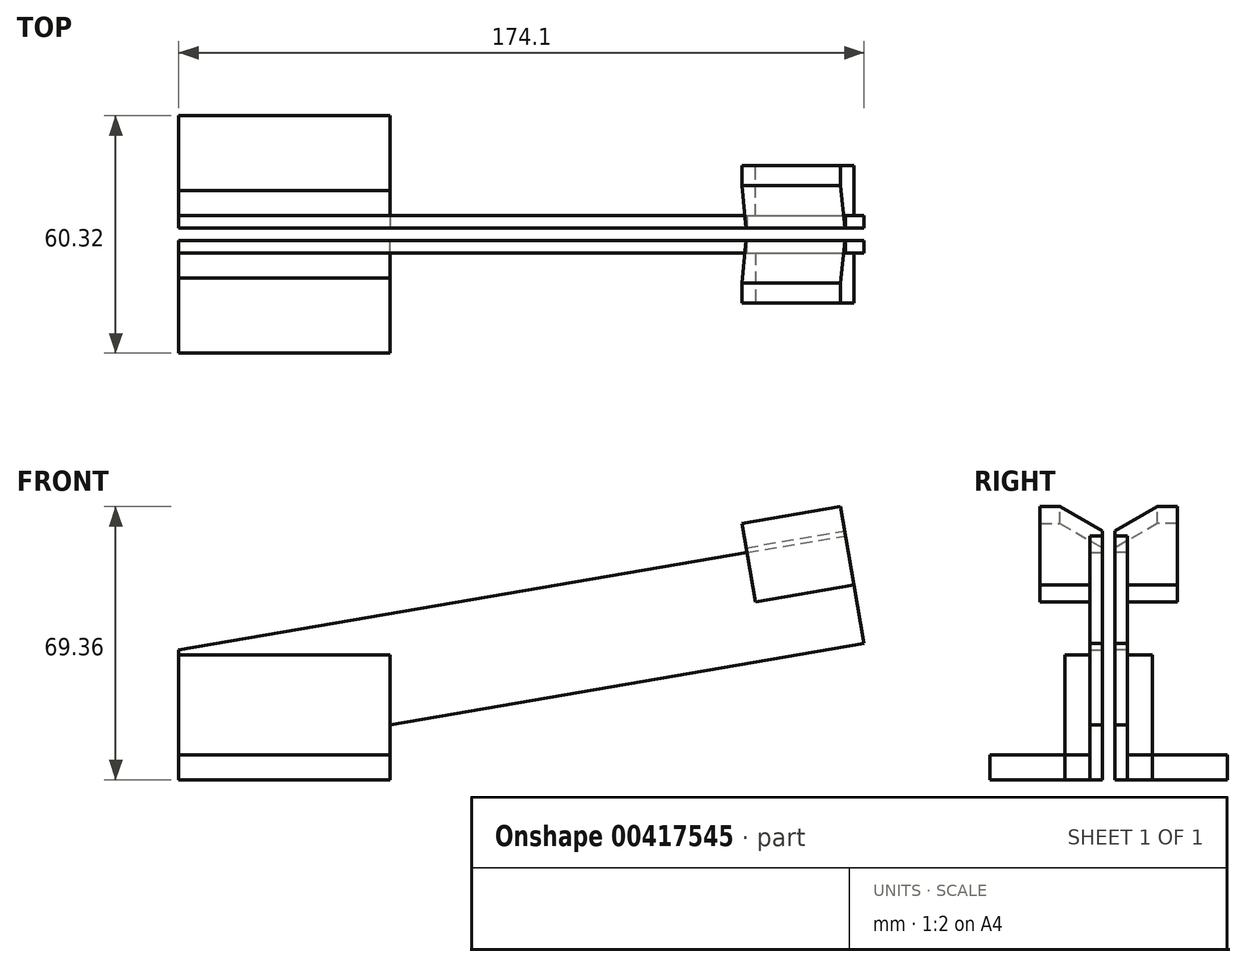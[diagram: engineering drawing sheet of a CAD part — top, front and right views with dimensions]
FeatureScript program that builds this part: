
annotation { "Feature Type Name" : "Feature", "Feature Type Description" : "" }
export const myFeature = defineFeature(function(context is Context, id is Id, definition is map)
    precondition{}
    {
        {
            var Q0;
            Q0=qCreatedBy(makeId("Front.planeOp"),FACE);
            var sketch = newSketch(context, id + "F0", { "sketchPlane" : qUnion([Q0])});
            skLineSegment(sketch, "E0", {"start": v(0, 0) * mm, "end": v(0, 33) * mm});
            skLineSegment(sketch, "E1", {"start": v(0, 33) * mm, "end": v(169.41, 61.97) * mm});
            skLineSegment(sketch, "E2", {"start": v(169.41, 61.97) * mm, "end": v(174.1, 34.58) * mm});
            skLineSegment(sketch, "E3", {"start": v(174.1, 34.58) * mm, "end": v(53.61, 13.97) * mm});
            skLineSegment(sketch, "E4", {"start": v(53.61, 13.97) * mm, "end": v(53.61, 0) * mm});
            skLineSegment(sketch, "E5", {"start": v(53.61, 0) * mm, "end": v(0, 0) * mm});
            skSolve(sketch);
        }
        {
            var Q0;
            Q0=makeQuery(id+"F0.imprint","IMPRINT",FACE,{"disambiguationData":[TD([[makeQuery(id+"F0.imprint","IMPRINT",EDGE,{"derivedFrom":sQuery(id+"F0.wireOp",EDGE,"E0")}),-1.0]])]});
            extrude(context, id + "F1", {"entities" : qUnion([Q0]), "depth" : 3.17 * mm});
        }
        {
            var Q0;
            Q0=makeQuery(id+"F1.opExtrude","SWEPT_FACE",FACE,{"disambiguationData":[OSD([sQuery(id+"F0.wireOp",EDGE,"E2")])]});
            var sketch = newSketch(context, id + "F2", { "sketchPlane" : qUnion([Q0])});
            skLineSegment(sketch, "E6", {"start": v(0, 32.52) * mm, "end": v(-3.18, 32.52) * mm});
            skLineSegment(sketch, "E7", {"start": v(-3.18, 32.52) * mm, "end": v(-3.17, 19.82) * mm});
            skLineSegment(sketch, "E8", {"start": v(-3.18, 19.82) * mm, "end": v(-15.88, 19.82) * mm});
            skLineSegment(sketch, "E9", {"start": v(-15.88, 19.82) * mm, "end": v(-15.88, 40.02) * mm});
            skLineSegment(sketch, "E10", {"start": v(-15.88, 40.02) * mm, "end": v(-10.8, 40.02) * mm});
            skLineSegment(sketch, "E11", {"start": v(-10.8, 40.02) * mm, "end": v(0, 33.79) * mm});
            skLineSegment(sketch, "E12", {"start": v(0, 33.79) * mm, "end": v(0, 32.52) * mm});
            skSolve(sketch);
        }
        {
            var Q0;
            Q0=makeQuery(id+"F2.imprint","IMPRINT",FACE,{"disambiguationData":[TD([[makeQuery(id+"F2.imprint","IMPRINT",EDGE,{"derivedFrom":sQuery(id+"F2.wireOp",EDGE,"E6")}),1.0]])]});
            extrude(context, id + "F3", {"entities" : qUnion([Q0]), "oppositeDirection" : true, "depth" : 25.4 * mm});
        }
        {
            var Q0;
            Q0=qCreatedBy(makeId("Front.planeOp"),FACE);
            cPlane(context, id + "F4", {"entities" : qUnion([Q0]), "cplaneType" : CPlaneType.OFFSET, "offset" : 1.59 * mm, "oppositeDirection" : true, "width" : 152.4 * mm, "height" : 152.4 * mm});
        }
        {
            var Q0;
            Q0=makeQuery(id+"F3.opExtrude","SWEPT_BODY",BODY,{"disambiguationData":[OSD([sQuery(id+"F2.wireOp",EDGE,"E6"),sQuery(id+"F2.wireOp",EDGE,"E7"),sQuery(id+"F2.wireOp",EDGE,"E8"),sQuery(id+"F2.wireOp",EDGE,"E9"),sQuery(id+"F2.wireOp",EDGE,"E10"),sQuery(id+"F2.wireOp",EDGE,"E11"),sQuery(id+"F2.wireOp",EDGE,"E12")])]});
            var Q1;
            Q1=makeQuery(id+"F1.opExtrude","SWEPT_BODY",BODY,{"disambiguationData":[OSD([sQuery(id+"F0.wireOp",EDGE,"E0"),sQuery(id+"F0.wireOp",EDGE,"E1"),sQuery(id+"F0.wireOp",EDGE,"E2"),sQuery(id+"F0.wireOp",EDGE,"E3"),sQuery(id+"F0.wireOp",EDGE,"E4"),sQuery(id+"F0.wireOp",EDGE,"E5")])]});
            var Q2;
            Q2=qCreatedBy(id+"F4.planeOp",FACE);
            mirror(context, id + "F5", {"entities" : qUnion([Q0, Q1]), "mirrorPlane" : qUnion([Q2])});
        }
        {
            var Q0;
            Q0=qCreatedBy(makeId("Top.planeOp"),FACE);
            var sketch = newSketch(context, id + "F6", { "sketchPlane" : qUnion([Q0])});
            skLineSegment(sketch, "E13.bottom", {"start": v(53.61, -28.57) * mm, "end": v(0, -28.57) * mm});
            skLineSegment(sketch, "E13.top", {"start": v(53.61, -3.18) * mm, "end": v(0, -3.18) * mm});
            skLineSegment(sketch, "E13.left", {"start": v(53.61, -28.58) * mm, "end": v(53.61, -3.18) * mm});
            skLineSegment(sketch, "E13.right", {"start": v(0, -28.57) * mm, "end": v(0, -3.18) * mm});
            skLineSegment(sketch, "E14.bottom", {"start": v(53.61, 31.75) * mm, "end": v(0, 31.75) * mm});
            skLineSegment(sketch, "E14.top", {"start": v(53.61, 6.35) * mm, "end": v(0, 6.35) * mm});
            skLineSegment(sketch, "E14.left", {"start": v(53.61, 31.75) * mm, "end": v(53.61, 6.35) * mm});
            skLineSegment(sketch, "E14.right", {"start": v(0, 31.75) * mm, "end": v(0, 6.35) * mm});
            skLineSegment(sketch, "E15", {"start": v(53.61, 12.7) * mm, "end": v(0, 12.7) * mm});
            skLineSegment(sketch, "E16", {"start": v(53.61, -9.53) * mm, "end": v(0, -9.53) * mm});
            skSolve(sketch);
        }
        {
            var Q0;
            Q0 = qSketchRegion(id + "F6", true);
            extrude(context, id + "F7", {"entities" : qUnion([Q0]), "depth" : 6.35 * mm});
        }
        {
            var Q0;
            {var subQ0=sQuery(id+"F6.wireOp",EDGE,"E14.top");Q0=makeQuery(id+"F6.imprint","IMPRINT",FACE,{"disambiguationData":[TD([[makeQuery(id+"F6.imprint","IMPRINT",EDGE,{"derivedFrom":subQ0}),-1.0]])]});}
            var Q1;
            {var subQ0=sQuery(id+"F6.wireOp",EDGE,"E13.top");Q1=makeQuery(id+"F6.imprint","IMPRINT",FACE,{"disambiguationData":[TD([[makeQuery(id+"F6.imprint","IMPRINT",EDGE,{"derivedFrom":subQ0}),1.0]])]});}
            extrude(context, id + "F8", {"entities" : qUnion([Q0, Q1]), "depth" : 31.75 * mm});
        }
    });
